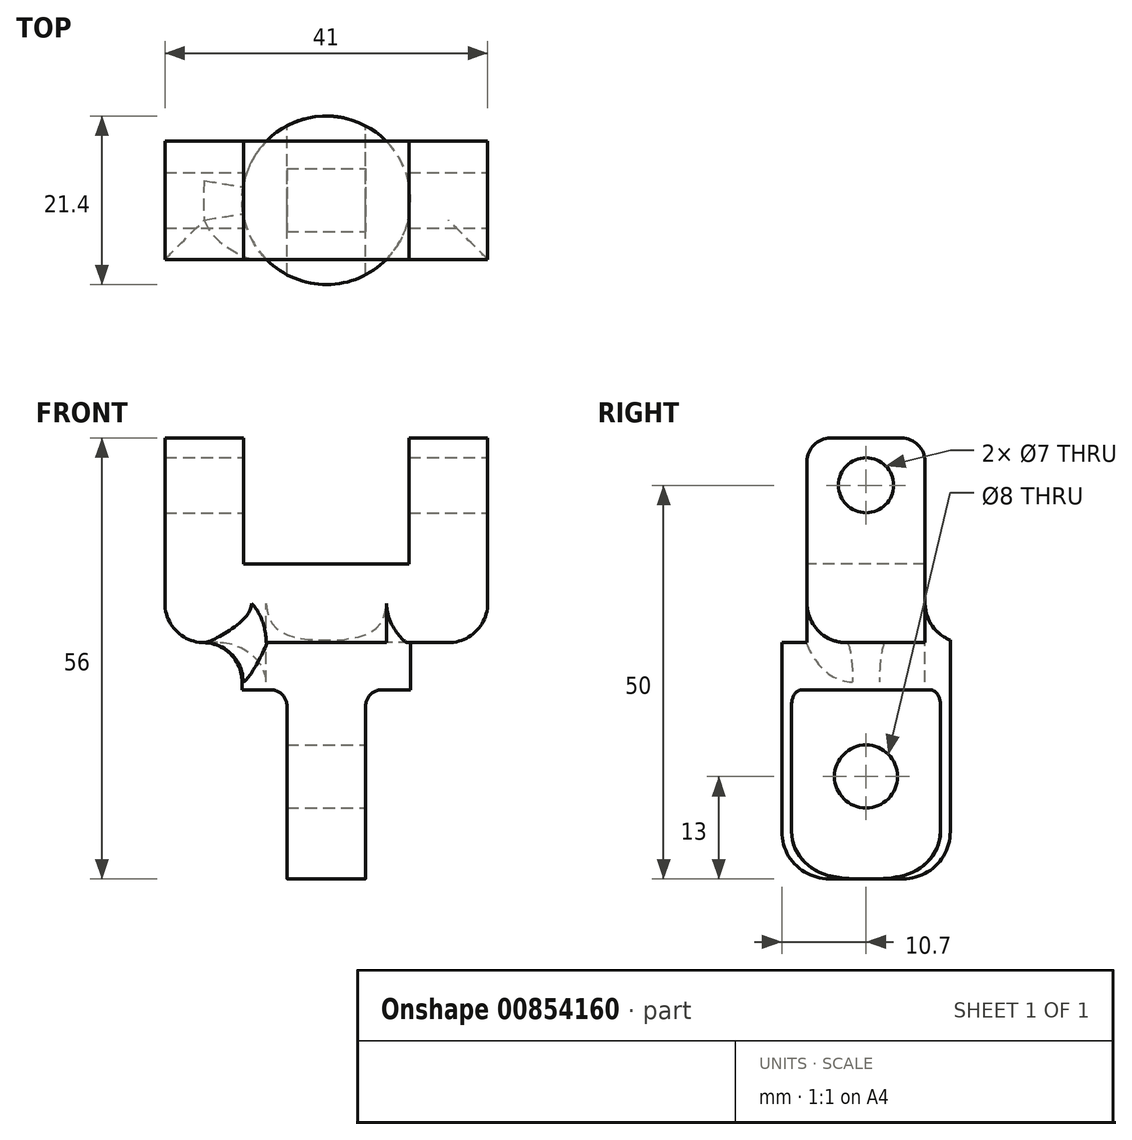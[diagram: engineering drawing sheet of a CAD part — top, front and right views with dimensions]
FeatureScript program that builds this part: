
annotation { "Feature Type Name" : "Feature", "Feature Type Description" : "" }
export const myFeature = defineFeature(function(context is Context, id is Id, definition is map)
    precondition{}
    {
        {
            var Q0;
            Q0=qCreatedBy(makeId("Top.planeOp"),FACE);
            var sketch = newSketch(context, id + "F0", { "sketchPlane" : qUnion([Q0])});
            skCircle(sketch, "E0", {"center": v(0, 0) * mm, "radius": 10.7 * mm});
            skSolve(sketch);
        }
        {
            var Q0;
            Q0=makeQuery(id+"F0.imprint","IMPRINT",FACE,{"disambiguationData":[TD([[makeQuery(id+"F0.imprint","IMPRINT",EDGE,{"derivedFrom":sQuery(id+"F0.wireOp",EDGE,"E0")}),1.0]])]});
            extrude(context, id + "F1", {"entities" : qUnion([Q0]), "oppositeDirection" : true, "depth" : 30 * mm, "offsetDistance" : 25 * mm});
        }
        {
            var Q0;
            Q0=makeQuery(id+"F1.opExtrude","CAP_EDGE",EDGE,{"disambiguationData":[OSD([sQuery(id+"F0.wireOp",EDGE,"E0")])],"isStart":false});
            fillet(context, id + "F2", {"entities" : qUnion([Q0]), "radius" : 6 * mm, "tangentPropagation" : true, "allowEdgeOverflow" : false});
        }
        {
            var Q0;
            Q0=makeQuery(id+"F1.opExtrude","CAP_FACE",FACE,{"disambiguationData":[OSD([sQuery(id+"F0.wireOp",EDGE,"E0")])],"isStart":true});
            var sketch = newSketch(context, id + "F3", { "sketchPlane" : qUnion([Q0])});
            skLineSegment(sketch, "E1.bottom", {"start": v(-20.5, -7.5) * mm, "end": v(20.5, -7.5) * mm});
            skLineSegment(sketch, "E1.top", {"start": v(-20.5, 7.5) * mm, "end": v(20.5, 7.5) * mm});
            skLineSegment(sketch, "E1.left", {"start": v(-20.5, -7.5) * mm, "end": v(-20.5, 7.5) * mm});
            skLineSegment(sketch, "E1.right", {"start": v(20.5, -7.5) * mm, "end": v(20.5, 7.5) * mm});
            skPoint(sketch, "E1.middle", {"position": v(0, 0) * mm});
            skSolve(sketch);
        }
        {
            var Q0;
            Q0=qSketchRegion(id+"F3",true);
            var Q1;
            Q1=qSketchRegion(id+"F5",true);
            extrude(context, id + "F4", {"entities" : qUnion([Q0, Q1]), "operationType" : NewBodyOperationType.ADD, "depth" : 10 * mm, "offsetDistance" : 25 * mm});
        }
        {
            var Q0;
            Q0=makeQuery(id+"F4.opExtrude","SWEPT_FACE",FACE,{"disambiguationData":[OSD([sQuery(id+"F3.wireOp",EDGE,"E1.top")])]});
            var sketch = newSketch(context, id + "F5", { "sketchPlane" : qUnion([Q0])});
            skPoint(sketch, "E2.orphan", {"position": v(20.5, 10) * mm});
            skPoint(sketch, "E3.orphan", {"position": v(-20.5, 0) * mm});
            skPoint(sketch, "E4.center.orphan", {"position": v(0, 5) * mm});
            skLineSegment(sketch, "E5.bottom", {"start": v(20.5, 10) * mm, "end": v(10.5, 10) * mm});
            skLineSegment(sketch, "E5.top", {"start": v(20.5, 26) * mm, "end": v(10.5, 26) * mm});
            skLineSegment(sketch, "E5.left", {"start": v(20.5, 10) * mm, "end": v(20.5, 26) * mm});
            skLineSegment(sketch, "E5.right", {"start": v(10.5, 10) * mm, "end": v(10.5, 26) * mm});
            skSolve(sketch);
        }
        {
            var Q0;
            {var subQ0=sQuery(id+"F5.wireOp",EDGE,"3WZYpcS9-OrWd-hupg-G2M5-sYLEi0oZUc7Y");var subQ1=sQuery(id+"F5.wireOp",EDGE,"kiMRuedf-Y1hH-4Eyv-ZV2F-Ktvl1FVyj3d9");var subQ2=makeQuery(id+"F5.imprint","INTERSECT",VERTEX,{"derivedFrom":[subQ1,subQ0]});Q0=makeQuery(id+"F5.imprint","IMPRINT",FACE,{"disambiguationData":[TD([[makeQuery(id+"F5.imprint","IMPRINT",EDGE,{"disambiguationData":[TD([[subQ2,-1.0]])],"derivedFrom":subQ1}),-1.0]])]});}
            var Q1;
            Q1=makeQuery(id+"F5.imprint","IMPRINT",FACE,{"disambiguationData":[TD([[makeQuery(id+"F5.imprint","IMPRINT",EDGE,{"derivedFrom":sQuery(id+"F5.wireOp",EDGE,"E5.bottom")}),-1.0]])]});
            extrude(context, id + "F6", {"entities" : qUnion([Q0, Q1]), "operationType" : NewBodyOperationType.ADD, "oppositeDirection" : true, "depth" : 15 * mm, "offsetDistance" : 25 * mm});
        }
        {
            var Q0;
            Q0=qCreatedBy(makeId("Right.planeOp"),FACE);
            var sketch = newSketch(context, id + "F7", { "sketchPlane" : qUnion([Q0])});
            skLineSegment(sketch, "E6", {"start": v(0, -17) * mm, "end": v(0, 0) * mm});
            skCircle(sketch, "E7", {"center": v(0, -17) * mm, "radius": 4 * mm});
            skSolve(sketch);
        }
        {
            var Q0;
            Q0=qSketchRegion(id+"F7",true);
            extrude(context, id + "F8", {"entities" : qUnion([Q0]), "operationType" : NewBodyOperationType.REMOVE, "endBound" : BoundingType.THROUGH_ALL, "oppositeDirection" : true, "depth" : 25 * mm, "offsetDistance" : 25 * mm});
        }
        {
            var Q0;
            Q0=makeQuery(id+"F8.boolean.opBoolean","COPY",FACE,{"derivedFrom":makeQuery(id+"F8.opExtrude","CAP_FACE",FACE,{"disambiguationData":[OSD([sQuery(id+"F7.wireOp",EDGE,"E7")])],"isStart":true})});
            extrude(context, id + "F9", {"entities" : qUnion([Q0]), "operationType" : NewBodyOperationType.REMOVE, "endBound" : BoundingType.THROUGH_ALL, "oppositeDirection" : true, "depth" : 25 * mm, "offsetDistance" : 25 * mm});
        }
        {
            var Q0;
            Q0=makeQuery(id+"F4.opExtrude","CAP_FACE",FACE,{"disambiguationData":[OSD([sQuery(id+"F3.wireOp",EDGE,"E1.bottom"),sQuery(id+"F3.wireOp",EDGE,"E1.top"),sQuery(id+"F3.wireOp",EDGE,"E1.left"),sQuery(id+"F3.wireOp",EDGE,"E1.right")])],"isStart":false});
            var sketch = newSketch(context, id + "F10", { "sketchPlane" : qUnion([Q0])});
            skLineSegment(sketch, "E8.bottom", {"start": v(20.5, 7.5) * mm, "end": v(10.5, 7.5) * mm});
            skLineSegment(sketch, "E8.top", {"start": v(20.5, -7.5) * mm, "end": v(10.5, -7.5) * mm});
            skLineSegment(sketch, "E8.left", {"start": v(20.5, 7.5) * mm, "end": v(20.5, -7.5) * mm});
            skLineSegment(sketch, "E8.right", {"start": v(10.5, 7.5) * mm, "end": v(10.5, -7.5) * mm});
            skSolve(sketch);
        }
        {
            var Q0;
            Q0=makeQuery(id+"F10.imprint","IMPRINT",FACE,{"disambiguationData":[TD([[makeQuery(id+"F10.imprint","IMPRINT",EDGE,{"derivedFrom":sQuery(id+"F10.wireOp",EDGE,"E8.bottom")}),-1.0]])]});
            extrude(context, id + "F11", {"entities" : qUnion([Q0]), "operationType" : NewBodyOperationType.ADD, "depth" : 16 * mm, "offsetDistance" : 25 * mm});
        }
        {
            var Q0;
            Q0=makeQuery(id+"F11.boolean.opBoolean","MERGE",FACE,{"derivedFrom":[makeQuery(id+"F4.opExtrude","SWEPT_FACE",FACE,{"disambiguationData":[OSD([sQuery(id+"F3.wireOp",EDGE,"E1.right")])]}),makeQuery(id+"F11.opExtrude","SWEPT_FACE",FACE,{"disambiguationData":[OSD([sQuery(id+"F10.wireOp",EDGE,"E8.left")])]})]});
            var sketch = newSketch(context, id + "F12", { "sketchPlane" : qUnion([Q0])});
            skLineSegment(sketch, "E9", {"start": v(0, 26) * mm, "end": v(0, 20) * mm});
            skCircle(sketch, "E10", {"center": v(0, 20) * mm, "radius": 2.5 * mm});
            skSolve(sketch);
        }
        {
            var Q0;
            Q0=makeQuery(id+"F4.opExtrude","CAP_EDGE",EDGE,{"disambiguationData":[OSD([sQuery(id+"F3.wireOp",EDGE,"E1.left")])],"isStart":true});
            var Q1;
            Q1=makeQuery(id+"F4.opExtrude","CAP_EDGE",EDGE,{"disambiguationData":[OSD([sQuery(id+"F3.wireOp",EDGE,"E1.right")])],"isStart":true});
            var Q2;
            {var subQ0=sQuery(id+"F3.wireOp",EDGE,"E1.bottom");Q2=makeQuery(id+"F4.boolean.opBoolean","SPLIT",EDGE,{"disambiguationData":[topologyDisambiguationEdgeConnected([makeQuery(id+"F1.opExtrude","CAP_FACE",FACE,{"disambiguationData":[OSD([sQuery(id+"F0.wireOp",EDGE,"E0")])],"isStart":true}),makeQuery(id+"F4.opExtrude","SWEPT_FACE",FACE,{"disambiguationData":[OSD([subQ0])]})])],"derivedFrom":makeQuery(id+"F4.opExtrude","CAP_EDGE",EDGE,{"disambiguationData":[OSD([subQ0])],"isStart":true})});}
            var Q3;
            {var subQ0=sQuery(id+"F3.wireOp",EDGE,"E1.top");Q3=makeQuery(id+"F4.boolean.opBoolean","SPLIT",EDGE,{"disambiguationData":[topologyDisambiguationEdgeConnected([makeQuery(id+"F1.opExtrude","CAP_FACE",FACE,{"disambiguationData":[OSD([sQuery(id+"F0.wireOp",EDGE,"E0")])],"isStart":true}),makeQuery(id+"F4.opExtrude","SWEPT_FACE",FACE,{"disambiguationData":[OSD([subQ0])]})])],"derivedFrom":makeQuery(id+"F4.opExtrude","CAP_EDGE",EDGE,{"disambiguationData":[OSD([subQ0])],"isStart":true})});}
            fillet(context, id + "F13", {"entities" : qUnion([Q0, Q1, Q2, Q3]), "radius" : 5 * mm, "tangentPropagation" : true, "allowEdgeOverflow" : false});
        }
        {
            var Q0;
            Q0=sQuery(id+"F12.wireOp",VERTEX,"E9.end");
            var Q1;
            Q1=makeQuery(id+"F1.opExtrude","SWEPT_BODY",BODY,{"disambiguationData":[OSD([sQuery(id+"F0.wireOp",EDGE,"E0")])]});
            hole(context, id + "F14", {"style" : HoleStyle.SIMPLE, "endStyle" : HoleEndStyle.THROUGH, "standardTappedOrClearance" : lookupTablePath({ "standard" : "ISO", "engagement" : "75%", "pitch" : "1 mm", "size" : "M8", "type" : "Tapped" }), "standardBlindInLast" : lookupTablePath({ "standard" : "ISO", "fit" : "Normal", "engagement" : "75%", "pitch" : "1 mm", "size" : "M8", "type" : "Clearance & tapped" }), "holeDiameter" : 7 * mm, "majorDiameter" : 8 * mm, "showTappedDepth" : true, "isTappedThrough" : true, "tappedDepth" : 12 * mm, "tapClearance" : 3, "locations" : qUnion([Q0]), "scope" : qUnion([Q1])});
        }
        {
            var Q0;
            Q0=makeQuery(id+"F13.opFillet","BLEND_EDGE",EDGE,{"blendedFrom":[makeQuery(id+"F4.opExtrude","CAP_EDGE",EDGE,{"disambiguationData":[OSD([sQuery(id+"F3.wireOp",EDGE,"E1.right")])],"isStart":true}),makeQuery(id+"F1.opExtrude","SWEPT_FACE",FACE,{"disambiguationData":[OSD([sQuery(id+"F0.wireOp",EDGE,"E0")])]})],"blendedInto":[makeQuery(id+"F1.opExtrude","SWEPT_FACE",FACE,{"disambiguationData":[OSD([sQuery(id+"F0.wireOp",EDGE,"E0")])]})]});
            var Q1;
            Q1=makeQuery(id+"F13.opFillet","BLEND_EDGE",EDGE,{"blendedFrom":[makeQuery(id+"F4.opExtrude","CAP_EDGE",EDGE,{"disambiguationData":[OSD([sQuery(id+"F3.wireOp",EDGE,"E1.left")])],"isStart":true}),makeQuery(id+"F1.opExtrude","SWEPT_FACE",FACE,{"disambiguationData":[OSD([sQuery(id+"F0.wireOp",EDGE,"E0")])]})],"blendedInto":[makeQuery(id+"F1.opExtrude","SWEPT_FACE",FACE,{"disambiguationData":[OSD([sQuery(id+"F0.wireOp",EDGE,"E0")])]})]});
            var Q2;
            {var subQ0=sQuery(id+"F0.wireOp",EDGE,"E0");Q2=makeQuery(id+"F4.boolean.opBoolean","SPLIT",EDGE,{"disambiguationData":[topologyDisambiguationEdgeConnected([makeQuery(id+"F1.opExtrude","SWEPT_FACE",FACE,{"disambiguationData":[OSD([subQ0])]}),makeQuery(id+"F4.opExtrude","CAP_FACE",FACE,{"disambiguationData":[OSD([sQuery(id+"F3.wireOp",EDGE,"E1.bottom"),sQuery(id+"F3.wireOp",EDGE,"E1.top"),sQuery(id+"F3.wireOp",EDGE,"E1.left"),sQuery(id+"F3.wireOp",EDGE,"E1.right")])],"isStart":true})]),OD(1.0)],"derivedFrom":makeQuery(id+"F1.opExtrude","CAP_EDGE",EDGE,{"disambiguationData":[OSD([subQ0])],"isStart":true})});}
            var Q3;
            {var subQ0=sQuery(id+"F0.wireOp",EDGE,"E0");Q3=makeQuery(id+"F4.boolean.opBoolean","SPLIT",EDGE,{"disambiguationData":[topologyDisambiguationEdgeConnected([makeQuery(id+"F1.opExtrude","SWEPT_FACE",FACE,{"disambiguationData":[OSD([subQ0])]}),makeQuery(id+"F4.opExtrude","CAP_FACE",FACE,{"disambiguationData":[OSD([sQuery(id+"F3.wireOp",EDGE,"E1.bottom"),sQuery(id+"F3.wireOp",EDGE,"E1.top"),sQuery(id+"F3.wireOp",EDGE,"E1.left"),sQuery(id+"F3.wireOp",EDGE,"E1.right")])],"isStart":true})]),OD(0.0)],"derivedFrom":makeQuery(id+"F1.opExtrude","CAP_EDGE",EDGE,{"disambiguationData":[OSD([subQ0])],"isStart":true})});}
            fillet(context, id + "F15", {"entities" : qUnion([Q0, Q1, Q2, Q3]), "radius" : 5 * mm, "tangentPropagation" : true, "allowEdgeOverflow" : false});
        }
        {
            var Q0;
            Q0=makeQuery(id+"F1.opExtrude","CAP_FACE",FACE,{"disambiguationData":[OSD([sQuery(id+"F0.wireOp",EDGE,"E0")])],"isStart":false});
            var sketch = newSketch(context, id + "F16", { "sketchPlane" : qUnion([Q0])});
            skLineSegment(sketch, "E11.bottom", {"start": v(5, 20) * mm, "end": v(-5, 20) * mm});
            skLineSegment(sketch, "E11.top", {"start": v(5, -20) * mm, "end": v(-5, -20) * mm});
            skLineSegment(sketch, "E11.left", {"start": v(5, 20) * mm, "end": v(5, -20) * mm});
            skLineSegment(sketch, "E11.right", {"start": v(-5, 20) * mm, "end": v(-5, -20) * mm});
            skPoint(sketch, "E11.middle", {"position": v(0, 0) * mm});
            skLineSegment(sketch, "E12.bottom", {"start": v(5, 20) * mm, "end": v(11.8, 20) * mm});
            skLineSegment(sketch, "E12.top", {"start": v(5, -20) * mm, "end": v(11.8, -20) * mm});
            skLineSegment(sketch, "E12.right", {"start": v(11.8, 20) * mm, "end": v(11.8, -20) * mm});
            skLineSegment(sketch, "E13.bottom", {"start": v(-5, 20) * mm, "end": v(-11.25, 20) * mm});
            skLineSegment(sketch, "E13.top", {"start": v(-5, -16.95) * mm, "end": v(-11.25, -16.95) * mm});
            skLineSegment(sketch, "E13.left", {"start": v(-5, 20) * mm, "end": v(-5, -16.95) * mm});
            skLineSegment(sketch, "E13.right", {"start": v(-11.25, 20) * mm, "end": v(-11.25, -16.95) * mm});
            skSolve(sketch);
        }
        {
            var Q0;
            {var subQ0=sQuery(id+"F16.wireOp",EDGE,"E13.bottom");Q0=makeQuery(id+"F16.imprint","IMPRINT",FACE,{"disambiguationData":[TD([[makeQuery(id+"F16.imprint","IMPRINT",EDGE,{"derivedFrom":subQ0}),1.0]])]});}
            var Q1;
            Q1=makeQuery(id+"F16.imprint","IMPRINT",FACE,{"disambiguationData":[TD([[makeQuery(id+"F16.imprint","IMPRINT",EDGE,{"derivedFrom":sQuery(id+"F16.wireOp",EDGE,"E11.left")}),1.0]])]});
            extrude(context, id + "F17", {"entities" : qUnion([Q0, Q1]), "operationType" : NewBodyOperationType.REMOVE, "oppositeDirection" : true, "depth" : 24 * mm, "offsetDistance" : 25 * mm});
        }
        {
            var Q0;
            Q0=makeQuery(id+"F17.boolean.opBoolean","COPY",EDGE,{"derivedFrom":makeQuery(id+"F17.opExtrude","CAP_EDGE",EDGE,{"disambiguationData":[OSD([sQuery(id+"F16.wireOp",EDGE,"E11.right")])],"isStart":false})});
            var Q1;
            Q1=makeQuery(id+"F17.boolean.opBoolean","COPY",EDGE,{"derivedFrom":makeQuery(id+"F17.opExtrude","CAP_EDGE",EDGE,{"disambiguationData":[OSD([sQuery(id+"F16.wireOp",EDGE,"E11.left")])],"isStart":false})});
            fillet(context, id + "F18", {"entities" : qUnion([Q0, Q1]), "radius" : 2 * mm, "tangentPropagation" : true, "allowEdgeOverflow" : false});
        }
        {
            var Q0;
            Q0=makeQuery(id+"F11.opExtrude","CAP_EDGE",EDGE,{"disambiguationData":[OSD([sQuery(id+"F10.wireOp",EDGE,"E8.right")])],"isStart":true});
            var Q1;
            Q1=makeQuery(id+"F6.opExtrude","SWEPT_EDGE",EDGE,{"disambiguationData":[OSD([sQuery(id+"F3.wireOp",EDGE,"E1.top"),sQuery(id+"F5.wireOp",EDGE,"E5.bottom"),sQuery(id+"F5.wireOp",EDGE,"E5.right")])]});
            var Q2;
            Q2=makeQuery(id+"F11.opExtrude","CAP_EDGE",EDGE,{"disambiguationData":[OSD([sQuery(id+"F10.wireOp",EDGE,"E8.top")])],"isStart":false});
            var Q3;
            Q3=makeQuery(id+"F6.opExtrude","CAP_EDGE",EDGE,{"disambiguationData":[OSD([sQuery(id+"F5.wireOp",EDGE,"E5.top")])],"isStart":false});
            var Q4;
            Q4=makeQuery(id+"F6.opExtrude","CAP_EDGE",EDGE,{"disambiguationData":[OSD([sQuery(id+"F5.wireOp",EDGE,"E5.top")])],"isStart":true});
            var Q5;
            Q5=makeQuery(id+"F11.opExtrude","CAP_EDGE",EDGE,{"disambiguationData":[OSD([sQuery(id+"F10.wireOp",EDGE,"E8.bottom")])],"isStart":false});
            fillet(context, id + "F19", {"entities" : qUnion([Q0, Q1, Q2, Q3, Q4, Q5]), "radius" : 3 * mm, "tangentPropagation" : true, "allowEdgeOverflow" : false});
        }
    });
